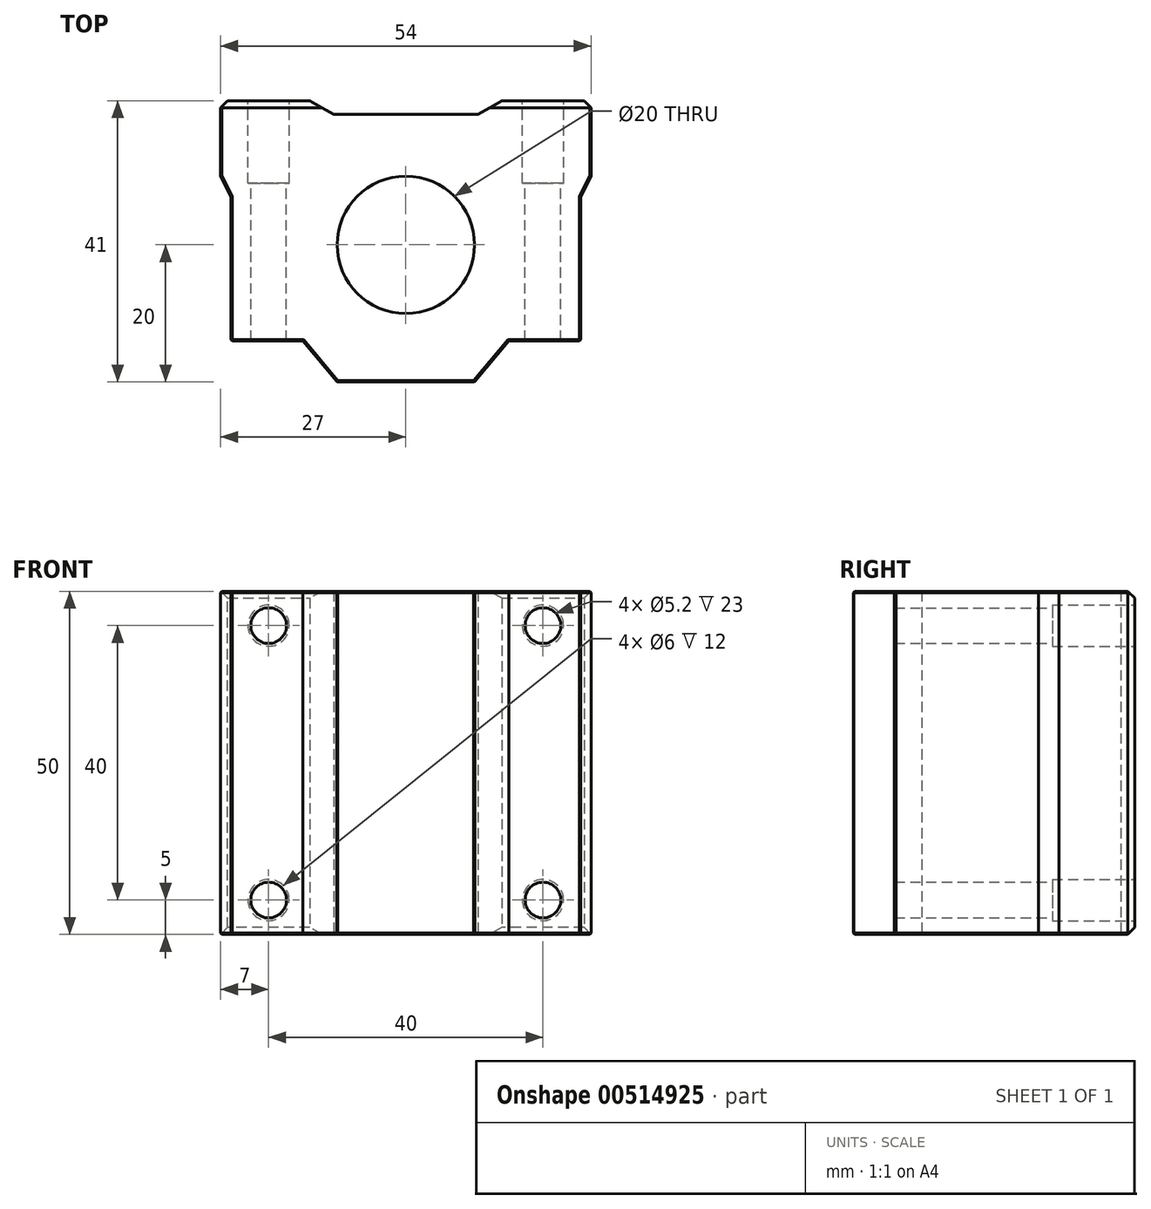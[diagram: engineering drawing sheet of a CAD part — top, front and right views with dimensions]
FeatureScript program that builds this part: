
annotation { "Feature Type Name" : "Feature", "Feature Type Description" : "" }
export const myFeature = defineFeature(function(context is Context, id is Id, definition is map)
    precondition{}
    {
        {
            var Q0;
            Q0=qCreatedBy(makeId("Top.planeOp"),FACE);
            var sketch = newSketch(context, id + "F0", { "sketchPlane" : qUnion([Q0])});
            skCircle(sketch, "E0", {"center": v(0, 0) * mm, "radius": 10 * mm});
            skLineSegment(sketch, "E1.bottom", {"start": v(-27, 21) * mm, "end": v(-14, 21) * mm});
            skLineSegment(sketch, "E1.left", {"start": v(-27, 21) * mm, "end": v(-27, 10) * mm});
            skLineSegment(sketch, "E1.right", {"start": v(27, 21) * mm, "end": v(27, 10) * mm});
            skLineSegment(sketch, "E2", {"start": v(-25.5, -14) * mm, "end": v(-15, -14) * mm});
            skLineSegment(sketch, "E3", {"start": v(-15, -14) * mm, "end": v(-10, -20) * mm});
            skLineSegment(sketch, "E4", {"start": v(25.5, -14) * mm, "end": v(15, -14) * mm});
            skLineSegment(sketch, "E5", {"start": v(15, -14) * mm, "end": v(10, -20) * mm});
            skLineSegment(sketch, "E6.left", {"start": v(-23, 21) * mm, "end": v(-23, -20) * mm, "construction": true});
            skLineSegment(sketch, "E6.right", {"start": v(-17, 21) * mm, "end": v(-17, -20) * mm, "construction": true});
            skLineSegment(sketch, "E7.left", {"start": v(17, 21) * mm, "end": v(17, -20) * mm, "construction": true});
            skLineSegment(sketch, "E7.right", {"start": v(23, 21) * mm, "end": v(23, -20) * mm, "construction": true});
            skLineSegment(sketch, "E8", {"start": v(-20, 33.26) * mm, "end": v(-20, -31.9) * mm, "construction": true});
            skLineSegment(sketch, "E9", {"start": v(20, 32.16) * mm, "end": v(20, -29.93) * mm, "construction": true});
            skLineSegment(sketch, "E10", {"start": v(-14, 21) * mm, "end": v(-10.5, 19) * mm});
            skLineSegment(sketch, "E11", {"start": v(-10.5, 19) * mm, "end": v(10.5, 19) * mm});
            skLineSegment(sketch, "E12", {"start": v(10.5, 19) * mm, "end": v(14, 21) * mm});
            skLineSegment(sketch, "E13", {"start": v(-27, 10) * mm, "end": v(-25.5, 7) * mm});
            skLineSegment(sketch, "E14", {"start": v(-25.5, 7) * mm, "end": v(-25.5, -14) * mm});
            skLineSegment(sketch, "E15.MirrorCS", {"start": v(27, 10) * mm, "end": v(25.5, 7) * mm});
            skLineSegment(sketch, "E16.MirrorCS", {"start": v(25.5, 7) * mm, "end": v(25.5, -14) * mm});
            skLineSegment(sketch, "E17.trimOffspring", {"start": v(-10, -20) * mm, "end": v(10, -20) * mm});
            skLineSegment(sketch, "E18", {"start": v(14, 21) * mm, "end": v(27, 21) * mm});
            skSolve(sketch);
        }
        {
            var Q0;
            Q0=makeQuery(id+"F0.imprint","IMPRINT",FACE,{"disambiguationData":[TD([[makeQuery(id+"F0.imprint","IMPRINT",EDGE,{"derivedFrom":sQuery(id+"F0.wireOp",EDGE,"E0")}),-1.0]])]});
            extrude(context, id + "F1", {"entities" : qUnion([Q0]), "endBound" : BoundingType.SYMMETRIC, "depth" : 50 * mm, "offsetDistance" : 25 * mm});
        }
        {
            var Q0;
            Q0=makeQuery(id+"F1.opExtrude","SWEPT_FACE",FACE,{"disambiguationData":[OSD([sQuery(id+"F0.wireOp",EDGE,"E1.bottom")])]});
            var sketch = newSketch(context, id + "F2", { "sketchPlane" : qUnion([Q0])});
            skPoint(sketch, "E19", {"position": v(20, -20) * mm});
            skPoint(sketch, "E20", {"position": v(20, 20) * mm});
            skPoint(sketch, "E21", {"position": v(-20, -20) * mm});
            skPoint(sketch, "E22", {"position": v(-20, 20) * mm});
            skSolve(sketch);
        }
        {
            var Q0;
            Q0=sQuery(id+"F2.wireOp",VERTEX,"E19");
            var Q1;
            Q1=sQuery(id+"F2.wireOp",VERTEX,"E20");
            var Q2;
            Q2=sQuery(id+"F2.wireOp",VERTEX,"E22");
            var Q3;
            Q3=sQuery(id+"F2.wireOp",VERTEX,"E21");
            var Q4;
            Q4=makeQuery(id+"F1.opExtrude","SWEPT_BODY",BODY,{"disambiguationData":[OSD([sQuery(id+"F0.wireOp",EDGE,"E0"),sQuery(id+"F0.wireOp",EDGE,"E1.bottom"),sQuery(id+"F0.wireOp",EDGE,"E1.left"),sQuery(id+"F0.wireOp",EDGE,"E1.right"),sQuery(id+"F0.wireOp",EDGE,"E2"),sQuery(id+"F0.wireOp",EDGE,"E3"),sQuery(id+"F0.wireOp",EDGE,"E4"),sQuery(id+"F0.wireOp",EDGE,"E5"),sQuery(id+"F0.wireOp",EDGE,"E10"),sQuery(id+"F0.wireOp",EDGE,"E11"),sQuery(id+"F0.wireOp",EDGE,"E12"),sQuery(id+"F0.wireOp",EDGE,"E13"),sQuery(id+"F0.wireOp",EDGE,"E14"),sQuery(id+"F0.wireOp",EDGE,"E15.MirrorCS"),sQuery(id+"F0.wireOp",EDGE,"E16.MirrorCS"),sQuery(id+"F0.wireOp",EDGE,"E17.trimOffspring"),sQuery(id+"F0.wireOp",EDGE,"E18")])]});
            hole(context, id + "F3", {"style" : HoleStyle.C_BORE, "endStyle" : HoleEndStyle.THROUGH, "holeDiameter" : 5.2 * mm, "cBoreDiameter" : 6 * mm, "cBoreDepth" : 12 * mm, "isTappedThrough" : true, "tappedDepth" : 12 * mm, "tapClearance" : 3, "locations" : qUnion([Q0, Q1, Q2, Q3]), "scope" : qUnion([Q4])});
        }
        {
            var Q0;
            Q0=makeQuery(id+"F1.opExtrude","SWEPT_EDGE",EDGE,{"disambiguationData":[OSD([sQuery(id+"F0.wireOp",EDGE,"E1.bottom"),sQuery(id+"F0.wireOp",EDGE,"E1.left")])]});
            var Q1;
            Q1=makeQuery(id+"F1.opExtrude","CAP_EDGE",EDGE,{"disambiguationData":[OSD([sQuery(id+"F0.wireOp",EDGE,"E1.bottom")])],"isStart":true});
            var Q2;
            Q2=makeQuery(id+"F1.opExtrude","CAP_EDGE",EDGE,{"disambiguationData":[OSD([sQuery(id+"F0.wireOp",EDGE,"E18")])],"isStart":true});
            var Q3;
            Q3=makeQuery(id+"F1.opExtrude","SWEPT_EDGE",EDGE,{"disambiguationData":[OSD([sQuery(id+"F0.wireOp",EDGE,"E1.right"),sQuery(id+"F0.wireOp",EDGE,"E18")])]});
            var Q4;
            Q4=makeQuery(id+"F1.opExtrude","CAP_EDGE",EDGE,{"disambiguationData":[OSD([sQuery(id+"F0.wireOp",EDGE,"E18")])],"isStart":false});
            var Q5;
            Q5=makeQuery(id+"F1.opExtrude","CAP_EDGE",EDGE,{"disambiguationData":[OSD([sQuery(id+"F0.wireOp",EDGE,"E1.bottom")])],"isStart":false});
            chamfer(context, id + "F4", {"entities" : qUnion([Q0, Q1, Q2, Q3, Q4, Q5]), "width" : 1 * mm, "tangentPropagation" : true});
        }
        {
            var Q0;
            Q0=makeQuery(id+"F1.opExtrude","SWEPT_EDGE",EDGE,{"disambiguationData":[OSD([sQuery(id+"F0.wireOp",EDGE,"E3"),sQuery(id+"F0.wireOp",EDGE,"E17.trimOffspring")])]});
            var Q1;
            Q1=makeQuery(id+"F1.opExtrude","SWEPT_EDGE",EDGE,{"disambiguationData":[OSD([sQuery(id+"F0.wireOp",EDGE,"E5"),sQuery(id+"F0.wireOp",EDGE,"E17.trimOffspring")])]});
            var Q2;
            Q2=makeQuery(id+"F1.opExtrude","SWEPT_EDGE",EDGE,{"disambiguationData":[OSD([sQuery(id+"F0.wireOp",EDGE,"E4"),sQuery(id+"F0.wireOp",EDGE,"E16.MirrorCS")])]});
            var Q3;
            Q3=makeQuery(id+"F1.opExtrude","CAP_EDGE",EDGE,{"disambiguationData":[OSD([sQuery(id+"F0.wireOp",EDGE,"E16.MirrorCS")])],"isStart":true});
            var Q4;
            Q4=makeQuery(id+"F1.opExtrude","CAP_EDGE",EDGE,{"disambiguationData":[OSD([sQuery(id+"F0.wireOp",EDGE,"E4")])],"isStart":true});
            var Q5;
            Q5=makeQuery(id+"F1.opExtrude","CAP_EDGE",EDGE,{"disambiguationData":[OSD([sQuery(id+"F0.wireOp",EDGE,"E5")])],"isStart":true});
            var Q6;
            Q6=makeQuery(id+"F1.opExtrude","CAP_EDGE",EDGE,{"disambiguationData":[OSD([sQuery(id+"F0.wireOp",EDGE,"E17.trimOffspring")])],"isStart":true});
            var Q7;
            Q7=makeQuery(id+"F1.opExtrude","CAP_EDGE",EDGE,{"disambiguationData":[OSD([sQuery(id+"F0.wireOp",EDGE,"E3")])],"isStart":true});
            var Q8;
            Q8=makeQuery(id+"F1.opExtrude","CAP_EDGE",EDGE,{"disambiguationData":[OSD([sQuery(id+"F0.wireOp",EDGE,"E2")])],"isStart":true});
            var Q9;
            Q9=makeQuery(id+"F1.opExtrude","CAP_EDGE",EDGE,{"disambiguationData":[OSD([sQuery(id+"F0.wireOp",EDGE,"E14")])],"isStart":true});
            var Q10;
            Q10=makeQuery(id+"F1.opExtrude","CAP_EDGE",EDGE,{"disambiguationData":[OSD([sQuery(id+"F0.wireOp",EDGE,"E13")])],"isStart":true});
            var Q11;
            Q11=makeQuery(id+"F1.opExtrude","CAP_EDGE",EDGE,{"disambiguationData":[OSD([sQuery(id+"F0.wireOp",EDGE,"E1.left")])],"isStart":true});
            var Q12;
            Q12=makeQuery(id+"F1.opExtrude","CAP_EDGE",EDGE,{"disambiguationData":[OSD([sQuery(id+"F0.wireOp",EDGE,"E1.right")])],"isStart":true});
            var Q13;
            Q13=makeQuery(id+"F1.opExtrude","CAP_EDGE",EDGE,{"disambiguationData":[OSD([sQuery(id+"F0.wireOp",EDGE,"E15.MirrorCS")])],"isStart":true});
            var Q14;
            Q14=makeQuery(id+"F1.opExtrude","CAP_EDGE",EDGE,{"disambiguationData":[OSD([sQuery(id+"F0.wireOp",EDGE,"E1.right")])],"isStart":false});
            var Q15;
            Q15=makeQuery(id+"F1.opExtrude","CAP_EDGE",EDGE,{"disambiguationData":[OSD([sQuery(id+"F0.wireOp",EDGE,"E16.MirrorCS")])],"isStart":false});
            var Q16;
            Q16=makeQuery(id+"F1.opExtrude","CAP_EDGE",EDGE,{"disambiguationData":[OSD([sQuery(id+"F0.wireOp",EDGE,"E15.MirrorCS")])],"isStart":false});
            var Q17;
            Q17=makeQuery(id+"F1.opExtrude","CAP_EDGE",EDGE,{"disambiguationData":[OSD([sQuery(id+"F0.wireOp",EDGE,"E4")])],"isStart":false});
            var Q18;
            Q18=makeQuery(id+"F1.opExtrude","CAP_EDGE",EDGE,{"disambiguationData":[OSD([sQuery(id+"F0.wireOp",EDGE,"E5")])],"isStart":false});
            var Q19;
            Q19=makeQuery(id+"F1.opExtrude","CAP_EDGE",EDGE,{"disambiguationData":[OSD([sQuery(id+"F0.wireOp",EDGE,"E17.trimOffspring")])],"isStart":false});
            var Q20;
            Q20=makeQuery(id+"F1.opExtrude","CAP_EDGE",EDGE,{"disambiguationData":[OSD([sQuery(id+"F0.wireOp",EDGE,"E3")])],"isStart":false});
            var Q21;
            Q21=makeQuery(id+"F1.opExtrude","CAP_EDGE",EDGE,{"disambiguationData":[OSD([sQuery(id+"F0.wireOp",EDGE,"E2")])],"isStart":false});
            var Q22;
            Q22=makeQuery(id+"F1.opExtrude","SWEPT_EDGE",EDGE,{"disambiguationData":[OSD([sQuery(id+"F0.wireOp",EDGE,"E2"),sQuery(id+"F0.wireOp",EDGE,"E14")])]});
            var Q23;
            Q23=makeQuery(id+"F1.opExtrude","CAP_EDGE",EDGE,{"disambiguationData":[OSD([sQuery(id+"F0.wireOp",EDGE,"E14")])],"isStart":false});
            var Q24;
            Q24=makeQuery(id+"F1.opExtrude","CAP_EDGE",EDGE,{"disambiguationData":[OSD([sQuery(id+"F0.wireOp",EDGE,"E1.left")])],"isStart":false});
            var Q25;
            Q25=makeQuery(id+"F1.opExtrude","CAP_EDGE",EDGE,{"disambiguationData":[OSD([sQuery(id+"F0.wireOp",EDGE,"E13")])],"isStart":false});
            chamfer(context, id + "F5", {"entities" : qUnion([Q0, Q1, Q2, Q3, Q4, Q5, Q6, Q7, Q8, Q9, Q10, Q11, Q12, Q13, Q14, Q15, Q16, Q17, Q18, Q19, Q20, Q21, Q22, Q23, Q24, Q25]), "width" : 0.2 * mm, "tangentPropagation" : true});
        }
    });
